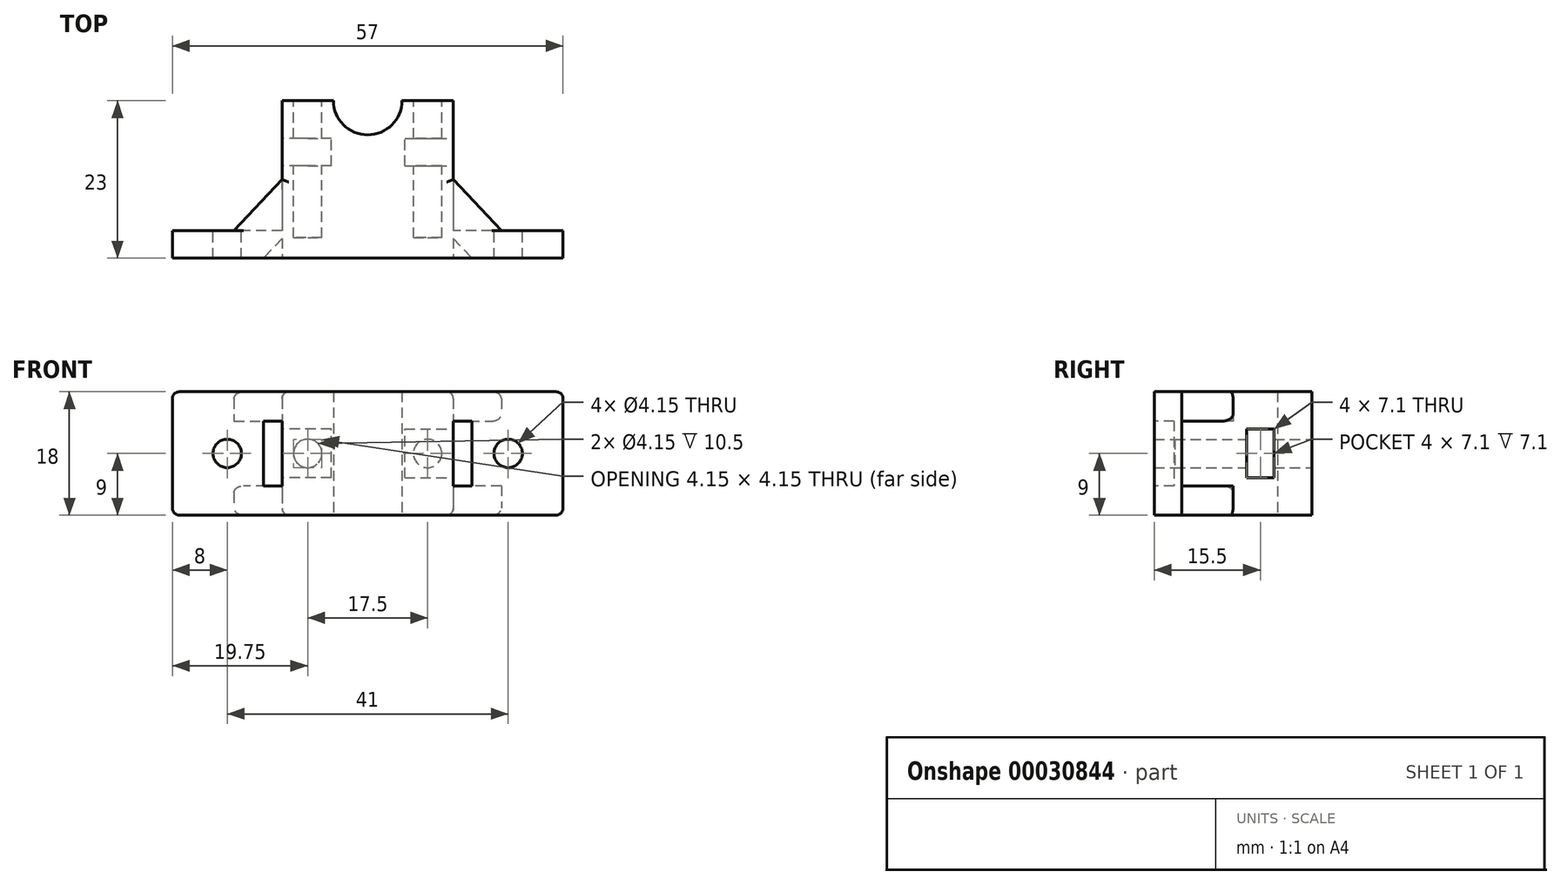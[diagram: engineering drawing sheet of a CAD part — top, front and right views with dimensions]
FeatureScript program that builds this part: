
annotation { "Feature Type Name" : "Feature", "Feature Type Description" : "" }
export const myFeature = defineFeature(function(context is Context, id is Id, definition is map)
    precondition{}
    {
        {
            var Q0;
            Q0=qCreatedBy(makeId("Top.planeOp"),FACE);
            var sketch = newSketch(context, id + "F0", { "sketchPlane" : qUnion([Q0])});
            skLineSegment(sketch, "E0.rect.bottom", {"start": v(12.5, -11.5) * mm, "end": v(-12.5, -11.5) * mm});
            skLineSegment(sketch, "E0.rect.top", {"start": v(12.5, 11.5) * mm, "end": v(5, 11.5) * mm});
            skLineSegment(sketch, "E0.rect.left", {"start": v(12.5, -11.5) * mm, "end": v(12.5, 11.5) * mm});
            skLineSegment(sketch, "E0.rect.right", {"start": v(-12.5, -11.5) * mm, "end": v(-12.5, 11.5) * mm});
            skPoint(sketch, "E0.rect.middle", {"position": v(0, 0) * mm});
            skArc(sketch, "E1", {"start": v(-5, 11.5) * mm, "mid": v(0, 6.5) * mm, "end": v(5, 11.5) * mm});
            skLineSegment(sketch, "E2.trimOffspring", {"start": v(-5, 11.5) * mm, "end": v(-12.5, 11.5) * mm});
            skLineSegment(sketch, "E3", {"start": v(12.5, -11.5) * mm, "end": v(28.5, -11.5) * mm});
            skLineSegment(sketch, "E4", {"start": v(28.5, -11.5) * mm, "end": v(28.5, -7.5) * mm});
            skLineSegment(sketch, "E5", {"start": v(28.5, -7.5) * mm, "end": v(19.5, -7.5) * mm});
            skLineSegment(sketch, "E6", {"start": v(19.5, -7.5) * mm, "end": v(12.5, 0) * mm});
            skLineSegment(sketch, "E7.MirrorCS", {"start": v(-19.5, -7.5) * mm, "end": v(-12.5, 0) * mm});
            skLineSegment(sketch, "E8.MirrorCS", {"start": v(-28.5, -7.5) * mm, "end": v(-19.5, -7.5) * mm});
            skLineSegment(sketch, "E9.MirrorCS", {"start": v(-28.5, -11.5) * mm, "end": v(-28.5, -7.5) * mm});
            skLineSegment(sketch, "E10.MirrorCS", {"start": v(-12.5, -11.5) * mm, "end": v(-28.5, -11.5) * mm});
            skSolve(sketch);
        }
        {
            var Q0;
            Q0=makeQuery(id+"F0.imprint","IMPRINT",FACE,{"disambiguationData":[TD([[makeQuery(id+"F0.imprint","IMPRINT",EDGE,{"derivedFrom":sQuery(id+"F0.wireOp",EDGE,"E0.rect.bottom")}),-1.0]])]});
            var Q1;
            {var subQ1=sQuery(id+"F0.wireOp",EDGE,"E3");Q1=makeQuery(id+"F0.imprint","IMPRINT",FACE,{"disambiguationData":[TD([[makeQuery(id+"F0.imprint","IMPRINT",EDGE,{"derivedFrom":subQ1}),1.0]])]});}
            var Q2;
            {var subQ1=sQuery(id+"F0.wireOp",EDGE,"E7.MirrorCS");Q2=makeQuery(id+"F0.imprint","IMPRINT",FACE,{"disambiguationData":[TD([[makeQuery(id+"F0.imprint","IMPRINT",EDGE,{"derivedFrom":subQ1}),-1.0]])]});}
            extrude(context, id + "F1", {"entities" : qUnion([Q0, Q1, Q2]), "depth" : 18 * mm});
        }
        {
            var Q0;
            Q0=makeQuery(id+"F1.opExtrude","SWEPT_FACE",FACE,{"disambiguationData":[OSD([sQuery(id+"F0.wireOp",EDGE,"E6")])]});
            var sketch = newSketch(context, id + "F2", { "sketchPlane" : qUnion([Q0])});
            skLineSegment(sketch, "E11", {"start": v(-18.79, 9) * mm, "end": v(-8.53, 9) * mm, "construction": true});
            skLineSegment(sketch, "E12.rect.bottom", {"start": v(-8.53, 4.27) * mm, "end": v(-18.79, 4.27) * mm});
            skLineSegment(sketch, "E12.rect.top", {"start": v(-8.53, 13.73) * mm, "end": v(-18.79, 13.73) * mm});
            skLineSegment(sketch, "E12.rect.left", {"start": v(-8.53, 4.27) * mm, "end": v(-8.53, 13.73) * mm});
            skLineSegment(sketch, "E12.rect.right", {"start": v(-18.79, 4.27) * mm, "end": v(-18.79, 13.73) * mm});
            skPoint(sketch, "E12.rect.middle", {"position": v(-13.66, 9) * mm});
            skSolve(sketch);
        }
        {
            var Q0;
            Q0=makeQuery(id+"F2.imprint","IMPRINT",FACE,{"disambiguationData":[TD([[makeQuery(id+"F2.imprint","IMPRINT",EDGE,{"derivedFrom":sQuery(id+"F2.wireOp",EDGE,"E12.rect.bottom")}),-1.0]])]});
            var Q1;
            Q1=makeQuery(id+"F1.opExtrude","SWEPT_FACE",FACE,{"disambiguationData":[OSD([sQuery(id+"F0.wireOp",EDGE,"E0.rect.left")])]});
            extrude(context, id + "F3", {"entities" : qUnion([Q0]), "operationType" : NewBodyOperationType.REMOVE, "endBound" : BoundingType.UP_TO_SURFACE, "oppositeDirection" : true, "endBoundEntityFace" : qUnion([Q1]), "depth" : 8 * mm});
        }
        {
            var Q0;
            Q0=makeQuery(id+"F3.boolean.opBoolean","COPY",FACE,{"derivedFrom":makeQuery(id+"F3.opExtrude","SWEPT_FACE",FACE,{"disambiguationData":[OSD([sQuery(id+"F2.wireOp",EDGE,"E12.rect.right")])]})});
            var Q1;
            Q1=makeQuery(id+"F1.opExtrude","SWEPT_FACE",FACE,{"disambiguationData":[OSD([sQuery(id+"F0.wireOp",EDGE,"E5")])]});
            extrude(context, id + "F4", {"entities" : qUnion([Q0]), "operationType" : NewBodyOperationType.ADD, "endBound" : BoundingType.UP_TO_SURFACE, "endBoundEntityFace" : qUnion([Q1]), "depth" : 25 * mm});
        }
        {
            var Q0;
            Q0=makeQuery(id+"F1.opExtrude","SWEPT_FACE",FACE,{"disambiguationData":[OSD([sQuery(id+"F0.wireOp",EDGE,"E7.MirrorCS")])]});
            var sketch = newSketch(context, id + "F5", { "sketchPlane" : qUnion([Q0])});
            skLineSegment(sketch, "E13", {"start": v(8.53, 9) * mm, "end": v(18.79, 9) * mm, "construction": true});
            skLineSegment(sketch, "E14.rect.bottom", {"start": v(18.79, 4.27) * mm, "end": v(8.53, 4.27) * mm});
            skLineSegment(sketch, "E14.rect.top", {"start": v(18.79, 13.73) * mm, "end": v(8.53, 13.73) * mm});
            skLineSegment(sketch, "E14.rect.left", {"start": v(18.79, 4.27) * mm, "end": v(18.79, 13.73) * mm});
            skLineSegment(sketch, "E14.rect.right", {"start": v(8.53, 4.27) * mm, "end": v(8.53, 13.73) * mm});
            skPoint(sketch, "E14.rect.middle", {"position": v(13.66, 9) * mm});
            skSolve(sketch);
        }
        {
            var Q0;
            Q0=makeQuery(id+"F5.imprint","IMPRINT",FACE,{"disambiguationData":[TD([[makeQuery(id+"F5.imprint","IMPRINT",EDGE,{"derivedFrom":sQuery(id+"F5.wireOp",EDGE,"E14.rect.bottom")}),-1.0]])]});
            var Q1;
            Q1=makeQuery(id+"F1.opExtrude","SWEPT_FACE",FACE,{"disambiguationData":[OSD([sQuery(id+"F0.wireOp",EDGE,"E0.rect.right")])]});
            extrude(context, id + "F6", {"entities" : qUnion([Q0]), "operationType" : NewBodyOperationType.REMOVE, "endBound" : BoundingType.UP_TO_SURFACE, "oppositeDirection" : true, "endBoundEntityFace" : qUnion([Q1]), "depth" : 25 * mm});
        }
        {
            var Q0;
            Q0=makeQuery(id+"F6.boolean.opBoolean","COPY",FACE,{"derivedFrom":makeQuery(id+"F6.opExtrude","SWEPT_FACE",FACE,{"disambiguationData":[OSD([sQuery(id+"F5.wireOp",EDGE,"E14.rect.left")])]})});
            var Q1;
            Q1=makeQuery(id+"F1.opExtrude","SWEPT_FACE",FACE,{"disambiguationData":[OSD([sQuery(id+"F0.wireOp",EDGE,"E8.MirrorCS")])]});
            extrude(context, id + "F7", {"entities" : qUnion([Q0]), "operationType" : NewBodyOperationType.ADD, "endBound" : BoundingType.UP_TO_SURFACE, "endBoundEntityFace" : qUnion([Q1]), "depth" : 25 * mm});
        }
        {
            var Q0;
            Q0=makeQuery(id+"F4.boolean.opBoolean","MERGE",FACE,{"derivedFrom":[makeQuery(id+"F1.opExtrude","SWEPT_FACE",FACE,{"disambiguationData":[OSD([sQuery(id+"F0.wireOp",EDGE,"E5")])]}),makeQuery(id+"F4.opExtrude","CAP_FACE",FACE,{"disambiguationData":[OSD([sQuery(id+"F2.wireOp",EDGE,"E12.rect.right")])],"isStart":false})]});
            var sketch = newSketch(context, id + "F8", { "sketchPlane" : qUnion([Q0])});
            skLineSegment(sketch, "E15", {"start": v(-28.5, 9) * mm, "end": v(-12.5, 9) * mm, "construction": true});
            skCircle(sketch, "E16", {"center": v(-20.5, 9) * mm, "radius": 2.08 * mm});
            skSolve(sketch);
        }
        {
            var Q0;
            Q0=makeQuery(id+"F7.boolean.opBoolean","MERGE",FACE,{"derivedFrom":[makeQuery(id+"F1.opExtrude","SWEPT_FACE",FACE,{"disambiguationData":[OSD([sQuery(id+"F0.wireOp",EDGE,"E8.MirrorCS")])]}),makeQuery(id+"F7.opExtrude","CAP_FACE",FACE,{"disambiguationData":[OSD([sQuery(id+"F5.wireOp",EDGE,"E14.rect.left")])],"isStart":false})]});
            var sketch = newSketch(context, id + "F9", { "sketchPlane" : qUnion([Q0])});
            skLineSegment(sketch, "E17", {"start": v(28.5, 9) * mm, "end": v(12.5, 9) * mm, "construction": true});
            skCircle(sketch, "E18", {"center": v(20.5, 9) * mm, "radius": 2.08 * mm});
            skSolve(sketch);
        }
        {
            var Q0;
            Q0=makeQuery(id+"F8.imprint","IMPRINT",FACE,{"disambiguationData":[TD([[makeQuery(id+"F8.imprint","IMPRINT",EDGE,{"derivedFrom":sQuery(id+"F8.wireOp",EDGE,"E16")}),1.0]])]});
            var Q1;
            Q1=makeQuery(id+"F9.imprint","IMPRINT",FACE,{"disambiguationData":[TD([[makeQuery(id+"F9.imprint","IMPRINT",EDGE,{"derivedFrom":sQuery(id+"F9.wireOp",EDGE,"E18")}),1.0]])]});
            extrude(context, id + "F10", {"entities" : qUnion([Q0, Q1]), "operationType" : NewBodyOperationType.REMOVE, "oppositeDirection" : true, "depth" : 25 * mm});
        }
        {
            var Q0;
            Q0=makeQuery(id+"F1.opExtrude","SWEPT_FACE",FACE,{"disambiguationData":[OSD([sQuery(id+"F0.wireOp",EDGE,"E0.rect.top")])]});
            var sketch = newSketch(context, id + "F11", { "sketchPlane" : qUnion([Q0])});
            skLineSegment(sketch, "E19", {"start": v(-12.5, 9) * mm, "end": v(-5, 9) * mm, "construction": true});
            skCircle(sketch, "E20", {"center": v(-8.75, 9) * mm, "radius": 2.08 * mm});
            skSolve(sketch);
        }
        {
            var Q0;
            Q0=makeQuery(id+"F1.opExtrude","SWEPT_FACE",FACE,{"disambiguationData":[OSD([sQuery(id+"F0.wireOp",EDGE,"E2.trimOffspring")])]});
            var sketch = newSketch(context, id + "F12", { "sketchPlane" : qUnion([Q0])});
            skLineSegment(sketch, "E21", {"start": v(5, 9) * mm, "end": v(12.5, 9) * mm, "construction": true});
            skCircle(sketch, "E22", {"center": v(8.75, 9) * mm, "radius": 2.08 * mm});
            skSolve(sketch);
        }
        {
            var Q0;
            Q0=makeQuery(id+"F11.imprint","IMPRINT",FACE,{"disambiguationData":[TD([[makeQuery(id+"F11.imprint","IMPRINT",EDGE,{"derivedFrom":sQuery(id+"F11.wireOp",EDGE,"E20")}),1.0]])]});
            var Q1;
            Q1=makeQuery(id+"F12.imprint","IMPRINT",FACE,{"disambiguationData":[TD([[makeQuery(id+"F12.imprint","IMPRINT",EDGE,{"derivedFrom":sQuery(id+"F12.wireOp",EDGE,"E22")}),1.0]])]});
            extrude(context, id + "F13", {"entities" : qUnion([Q0, Q1]), "operationType" : NewBodyOperationType.REMOVE, "oppositeDirection" : true, "depth" : 20 * mm});
        }
        {
            var Q0;
            Q0=makeQuery(id+"F6.boolean.opBoolean","MERGE",FACE,{"derivedFrom":[makeQuery(id+"F1.opExtrude","SWEPT_FACE",FACE,{"disambiguationData":[OSD([sQuery(id+"F0.wireOp",EDGE,"E0.rect.right")])]}),makeQuery(id+"F6.opExtrude","CAP_FACE",FACE,{"disambiguationData":[OSD([sQuery(id+"F5.wireOp",EDGE,"E14.rect.bottom"),sQuery(id+"F5.wireOp",EDGE,"E14.rect.top"),sQuery(id+"F5.wireOp",EDGE,"E14.rect.left"),sQuery(id+"F5.wireOp",EDGE,"E14.rect.right")])],"isStart":false})]});
            var sketch = newSketch(context, id + "F14", { "sketchPlane" : qUnion([Q0])});
            skLineSegment(sketch, "E23.rect.bottom", {"start": v(-2, 5.45) * mm, "end": v(-6, 5.45) * mm});
            skLineSegment(sketch, "E23.rect.top", {"start": v(-2, 12.55) * mm, "end": v(-6, 12.55) * mm});
            skLineSegment(sketch, "E23.rect.left", {"start": v(-2, 5.45) * mm, "end": v(-2, 12.55) * mm});
            skLineSegment(sketch, "E23.rect.right", {"start": v(-6, 5.45) * mm, "end": v(-6, 12.55) * mm});
            skPoint(sketch, "E23.rect.middle", {"position": v(-4, 9) * mm});
            skLineSegment(sketch, "E24", {"start": v(-4, 9) * mm, "end": v(-11.5, 9) * mm, "construction": true});
            skSolve(sketch);
        }
        {
            var Q0;
            Q0=makeQuery(id+"F14.imprint","IMPRINT",FACE,{"disambiguationData":[TD([[makeQuery(id+"F14.imprint","IMPRINT",EDGE,{"derivedFrom":sQuery(id+"F14.wireOp",EDGE,"E23.rect.bottom")}),-1.0]])]});
            extrude(context, id + "F15", {"entities" : qUnion([Q0]), "operationType" : NewBodyOperationType.REMOVE, "oppositeDirection" : true, "depth" : 7.2 * mm});
        }
        {
            var Q0;
            Q0=makeQuery(id+"F3.boolean.opBoolean","MERGE",FACE,{"derivedFrom":[makeQuery(id+"F1.opExtrude","SWEPT_FACE",FACE,{"disambiguationData":[OSD([sQuery(id+"F0.wireOp",EDGE,"E0.rect.left")])]}),makeQuery(id+"F3.opExtrude","CAP_FACE",FACE,{"disambiguationData":[OSD([sQuery(id+"F2.wireOp",EDGE,"E12.rect.bottom"),sQuery(id+"F2.wireOp",EDGE,"E12.rect.top"),sQuery(id+"F2.wireOp",EDGE,"E12.rect.left"),sQuery(id+"F2.wireOp",EDGE,"E12.rect.right")])],"isStart":false})]});
            var sketch = newSketch(context, id + "F16", { "sketchPlane" : qUnion([Q0])});
            skLineSegment(sketch, "E25", {"start": v(11.5, 9) * mm, "end": v(4, 9) * mm, "construction": true});
            skLineSegment(sketch, "E26.rect.bottom", {"start": v(2, 5.45) * mm, "end": v(6, 5.45) * mm});
            skLineSegment(sketch, "E26.rect.top", {"start": v(2, 12.55) * mm, "end": v(6, 12.55) * mm});
            skLineSegment(sketch, "E26.rect.left", {"start": v(2, 5.45) * mm, "end": v(2, 12.55) * mm});
            skLineSegment(sketch, "E26.rect.right", {"start": v(6, 5.45) * mm, "end": v(6, 12.55) * mm});
            skPoint(sketch, "E26.rect.middle", {"position": v(4, 9) * mm});
            skSolve(sketch);
        }
        {
            var Q0;
            Q0=makeQuery(id+"F16.imprint","IMPRINT",FACE,{"disambiguationData":[TD([[makeQuery(id+"F16.imprint","IMPRINT",EDGE,{"derivedFrom":sQuery(id+"F16.wireOp",EDGE,"E26.rect.bottom")}),1.0]])]});
            extrude(context, id + "F17", {"entities" : qUnion([Q0]), "operationType" : NewBodyOperationType.REMOVE, "oppositeDirection" : true, "depth" : 7.1 * mm});
        }
        {
            var Q0;
            Q0=makeQuery(id+"F1.opExtrude","CAP_EDGE",EDGE,{"disambiguationData":[OSD([sQuery(id+"F0.wireOp",EDGE,"E0.rect.right")])],"isStart":false});
            var Q1;
            Q1=makeQuery(id+"F1.opExtrude","CAP_EDGE",EDGE,{"disambiguationData":[OSD([sQuery(id+"F0.wireOp",EDGE,"E4")])],"isStart":false});
            var Q2;
            Q2=makeQuery(id+"F1.opExtrude","CAP_EDGE",EDGE,{"disambiguationData":[OSD([sQuery(id+"F0.wireOp",EDGE,"E0.rect.left")])],"isStart":false});
            var Q3;
            Q3=makeQuery(id+"F1.opExtrude","CAP_EDGE",EDGE,{"disambiguationData":[OSD([sQuery(id+"F0.wireOp",EDGE,"E9.MirrorCS")])],"isStart":false});
            var Q4;
            Q4=makeQuery(id+"F1.opExtrude","CAP_EDGE",EDGE,{"disambiguationData":[OSD([sQuery(id+"F0.wireOp",EDGE,"E9.MirrorCS")])],"isStart":true});
            var Q5;
            Q5=makeQuery(id+"F1.opExtrude","CAP_EDGE",EDGE,{"disambiguationData":[OSD([sQuery(id+"F0.wireOp",EDGE,"E0.rect.right")])],"isStart":true});
            var Q6;
            Q6=makeQuery(id+"F1.opExtrude","CAP_EDGE",EDGE,{"disambiguationData":[OSD([sQuery(id+"F0.wireOp",EDGE,"E0.rect.left")])],"isStart":true});
            var Q7;
            Q7=makeQuery(id+"F1.opExtrude","CAP_EDGE",EDGE,{"disambiguationData":[OSD([sQuery(id+"F0.wireOp",EDGE,"E4")])],"isStart":true});
            fillet(context, id + "F18", {"entities" : qUnion([Q0, Q1, Q2, Q3, Q4, Q5, Q6, Q7]), "radius" : 1 * mm, "tangentPropagation" : true, "allowEdgeOverflow" : false});
        }
        {
            var Q0;
            Q0=makeQuery(id+"F1.opExtrude","CAP_EDGE",EDGE,{"disambiguationData":[OSD([sQuery(id+"F0.wireOp",EDGE,"E7.MirrorCS")])],"isStart":true});
            var Q1;
            Q1=makeQuery(id+"F6.boolean.opBoolean","COPY",EDGE,{"derivedFrom":makeQuery(id+"F6.opExtrude","CAP_EDGE",EDGE,{"disambiguationData":[OSD([sQuery(id+"F5.wireOp",EDGE,"E14.rect.top")])],"isStart":true})});
            var Q2;
            Q2=makeQuery(id+"F1.opExtrude","CAP_EDGE",EDGE,{"disambiguationData":[OSD([sQuery(id+"F0.wireOp",EDGE,"E7.MirrorCS")])],"isStart":false});
            var Q3;
            Q3=makeQuery(id+"F6.boolean.opBoolean","COPY",EDGE,{"derivedFrom":makeQuery(id+"F6.opExtrude","CAP_EDGE",EDGE,{"disambiguationData":[OSD([sQuery(id+"F5.wireOp",EDGE,"E14.rect.bottom")])],"isStart":true})});
            var Q4;
            Q4=makeQuery(id+"F1.opExtrude","CAP_EDGE",EDGE,{"disambiguationData":[OSD([sQuery(id+"F0.wireOp",EDGE,"E6")])],"isStart":true});
            var Q5;
            Q5=makeQuery(id+"F3.boolean.opBoolean","COPY",EDGE,{"derivedFrom":makeQuery(id+"F3.opExtrude","CAP_EDGE",EDGE,{"disambiguationData":[OSD([sQuery(id+"F2.wireOp",EDGE,"E12.rect.bottom")])],"isStart":true})});
            var Q6;
            Q6=makeQuery(id+"F3.boolean.opBoolean","COPY",EDGE,{"derivedFrom":makeQuery(id+"F3.opExtrude","CAP_EDGE",EDGE,{"disambiguationData":[OSD([sQuery(id+"F2.wireOp",EDGE,"E12.rect.top")])],"isStart":true})});
            var Q7;
            Q7=makeQuery(id+"F1.opExtrude","CAP_EDGE",EDGE,{"disambiguationData":[OSD([sQuery(id+"F0.wireOp",EDGE,"E6")])],"isStart":false});
            fillet(context, id + "F19", {"entities" : qUnion([Q0, Q1, Q2, Q3, Q4, Q5, Q6, Q7]), "radius" : 1 * mm, "tangentPropagation" : true, "allowEdgeOverflow" : false});
        }
    });
